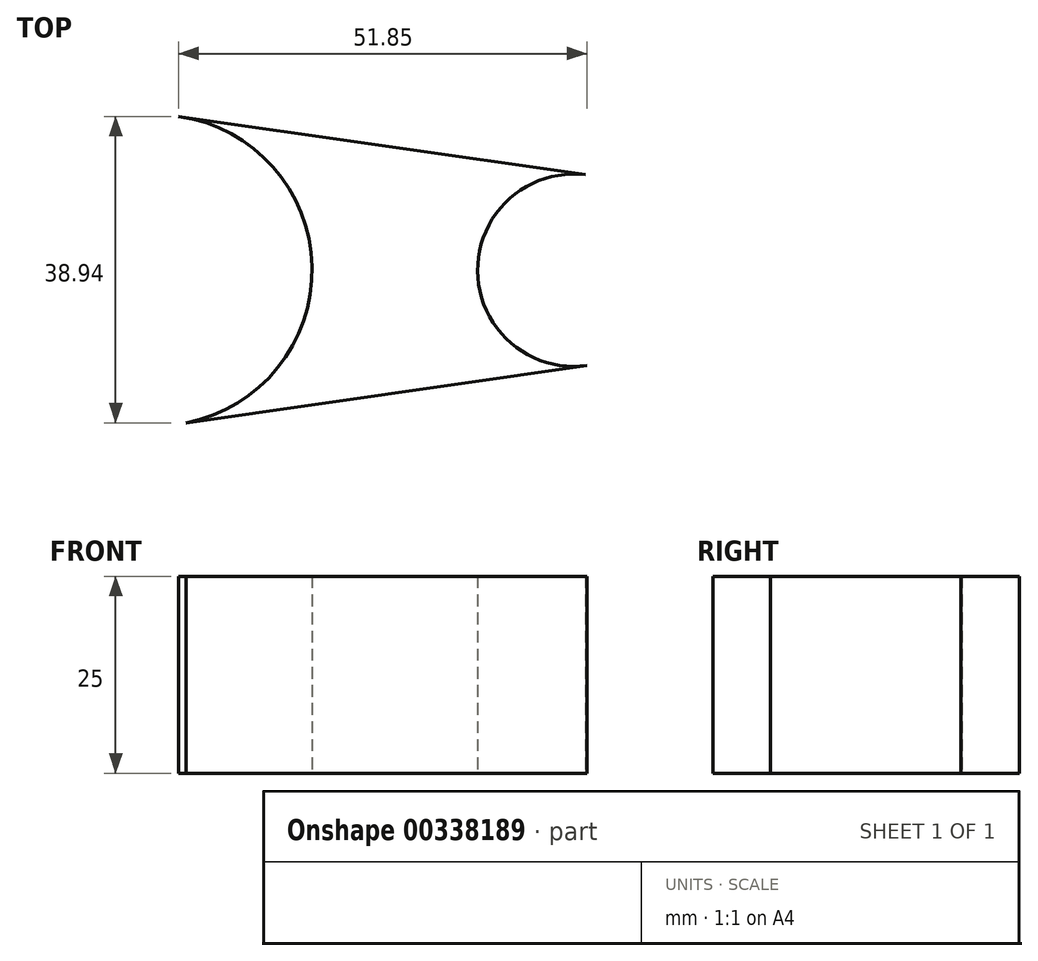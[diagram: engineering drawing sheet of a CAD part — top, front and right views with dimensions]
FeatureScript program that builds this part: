
annotation { "Feature Type Name" : "Feature", "Feature Type Description" : "" }
export const myFeature = defineFeature(function(context is Context, id is Id, definition is map)
    precondition{}
    {
        {
            var Q0;
            Q0=qCreatedBy(makeId("Top.planeOp"),FACE);
            var sketch = newSketch(context, id + "F0", { "sketchPlane" : qUnion([Q0])});
            skCircle(sketch, "E0", {"center": v(-33.36, 0) * mm, "radius": 19.75 * mm});
            skCircle(sketch, "E1", {"center": v(19.63, 0) * mm, "radius": 12.22 * mm});
            skLineSegment(sketch, "E2", {"start": v(-30.55, 19.55) * mm, "end": v(21.12, 12.13) * mm});
            skLineSegment(sketch, "E3", {"start": v(-31.52, -19.66) * mm, "end": v(21.43, -12.09) * mm});
            skSolve(sketch);
        }
        {
            var Q0;
            Q0 = qSketchRegion(id + "F0", true);
            var sketch = newSketch(context, id + "F1", { "sketchPlane" : qUnion([Q0])});
            skCircle(sketch, "E4", {"center": v(-20.25, 32.76) * mm, "radius": 5 * mm});
            skSolve(sketch);
        }
        {
            var Q0;
            {var subQ5=sQuery(id+"F0.wireOp",EDGE,"E2");Q0=makeQuery(id+"F0.imprint","IMPRINT",FACE,{"disambiguationData":[TD([[makeQuery(id+"F0.imprint","IMPRINT",EDGE,{"derivedFrom":subQ5}),-1.0]])]});}
            var Q1;
            {var subQ0=sQuery(id+"F0.wireOp",EDGE,"E0");var subQ1=makeQuery(id+"F0.imprint","INTERSECT",VERTEX,{"derivedFrom":[subQ0,sQuery(id+"F0.wireOp",EDGE,"E2")]});Q1=makeQuery(id+"F1.imprint","IMPRINT",FACE,{"disambiguationData":[TD([[makeQuery(id+"F1.imprint","IMPRINT",EDGE,{"derivedFrom":makeQuery(id+"F0.imprint","IMPRINT",EDGE,{"disambiguationData":[TD([[subQ1,-1.0]])],"derivedFrom":subQ0})}),1.0]])]});}
            extrude(context, id + "F2", {"entities" : qUnion([Q0, Q1]), "depth" : 25 * mm});
        }
    });
